# Revit family: P191568KX-049c_KCED606G
name_source: partatom
category: Specialty Equipment
units: mm (PartAtom-declared; Revit-internal decimal feet)

## family parameters
Always vertical = Yes
Cut with Voids When Loaded = No
Enable Cutting in Views = No
Maintain Annotation Orientation = No
Part Type = Normal
Room Calculation Point = No
Round Connector Dimension = Use Diameter
Shared = No
Work Plane-Based = No

## types (2) — shared parameters
Amps = 0 A
Body Material = ARCAT - Metal - Steel - Stainless
Cooktop Material = ARCAT - Glass - Black
Default Elevation = 0"
Depth = 22 1/16"
Description = 36" Electric Downdraft Cooktop with 5 Elements
Table de cuisson électrique à évacuation descendante et 5 éléments, 36 po
Dimension Guide = http://access.whirlpool.com Guide&sku=KCED606GBL&language=EN
http://access.whirlpool.com Guide&sku=KCED606GBL&language=EN
Family Name = COOKING
Feature 1 = Downdraft Ventilation
Ventilation à évacuation descendante
Feature 2 = 10'' Even-Heat™ Ultra Element with Simmer Setting
Élément Even-Heat™ Ultra de 10 po avec fonction de mijotage
Feature 3 = 6'' Even-Heat™ Element with Melt Setting
Élément Even-Heat™ de 6 po avec fonction de fonte
Grid Material = ARCAT - Metal - Steel - Black
Height = 3 21/32"
Installation-Fabrication = http://access.whirlpool.com Instruction&sku=KCED606GBL&language=EN
http://access.whirlpool.com Instruction&sku=KCED606GBL&language=FR
Knob Material = ARCAT - Metal - Steel - Gray
Manufacturer = KitchenAid
Voltage = 0 V
Width = 36 5/16"

## type names
- KCED606GSS
- KCED606GBL

note: column(s) folded — value = type name in every type: Model
type visibility flags: 2 boolean params named "<type name>" — each type sets only its own to Yes (folded from table)

## geometry (parser evidence)
native form markers: Sweep x3
no freeform markers — native parametric forms only
